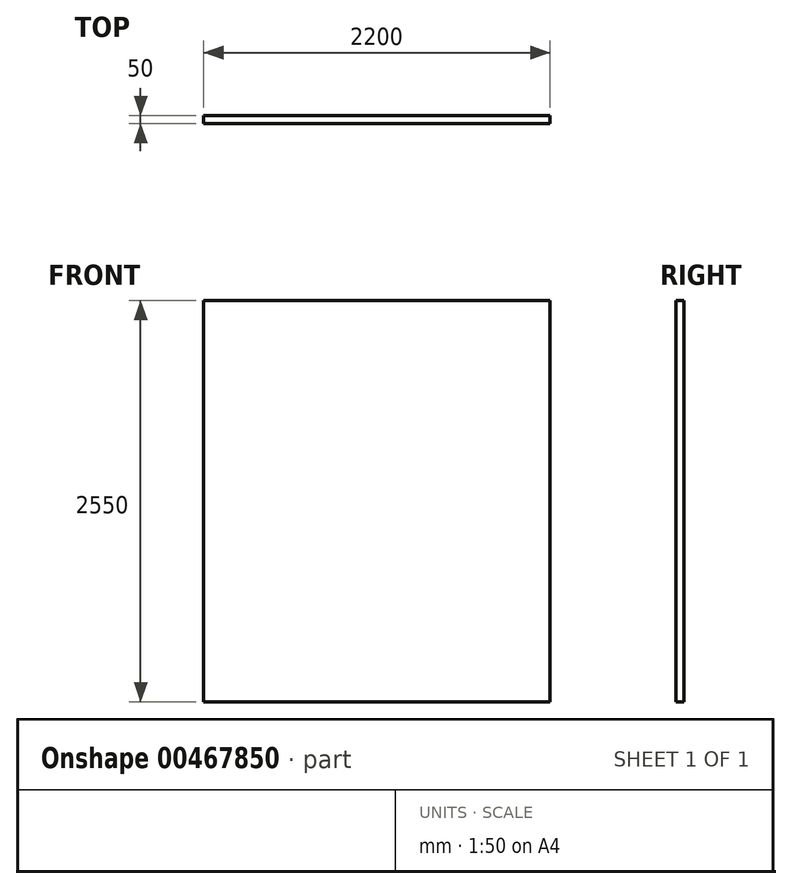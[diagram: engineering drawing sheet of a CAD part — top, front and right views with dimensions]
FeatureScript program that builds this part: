
annotation { "Feature Type Name" : "Feature", "Feature Type Description" : "" }
export const myFeature = defineFeature(function(context is Context, id is Id, definition is map)
    precondition{}
    {
        {
            var Q0;
            Q0=qCreatedBy(makeId("Front.planeOp"),FACE);
            var sketch = newSketch(context, id + "F0", { "sketchPlane" : qUnion([Q0])});
            skLineSegment(sketch, "E0.bottom", {"start": v(1100, -1275) * mm, "end": v(-1100, -1275) * mm});
            skLineSegment(sketch, "E0.top", {"start": v(1100, 1275) * mm, "end": v(-1100, 1275) * mm});
            skLineSegment(sketch, "E0.left", {"start": v(1100, -1275) * mm, "end": v(1100, 1275) * mm});
            skLineSegment(sketch, "E0.right", {"start": v(-1100, -1275) * mm, "end": v(-1100, 1275) * mm});
            skPoint(sketch, "E0.middle", {"position": v(0, 0) * mm});
            skSolve(sketch);
        }
        {
            var Q0;
            Q0=makeQuery(id+"F0.imprint","IMPRINT",FACE,{"disambiguationData":[TD([[makeQuery(id+"F0.imprint","IMPRINT",EDGE,{"derivedFrom":sQuery(id+"F0.wireOp",EDGE,"E0.bottom")}),-1.0]])]});
            extrude(context, id + "F1", {"entities" : qUnion([Q0]), "depth" : 50 * mm});
        }
    });
